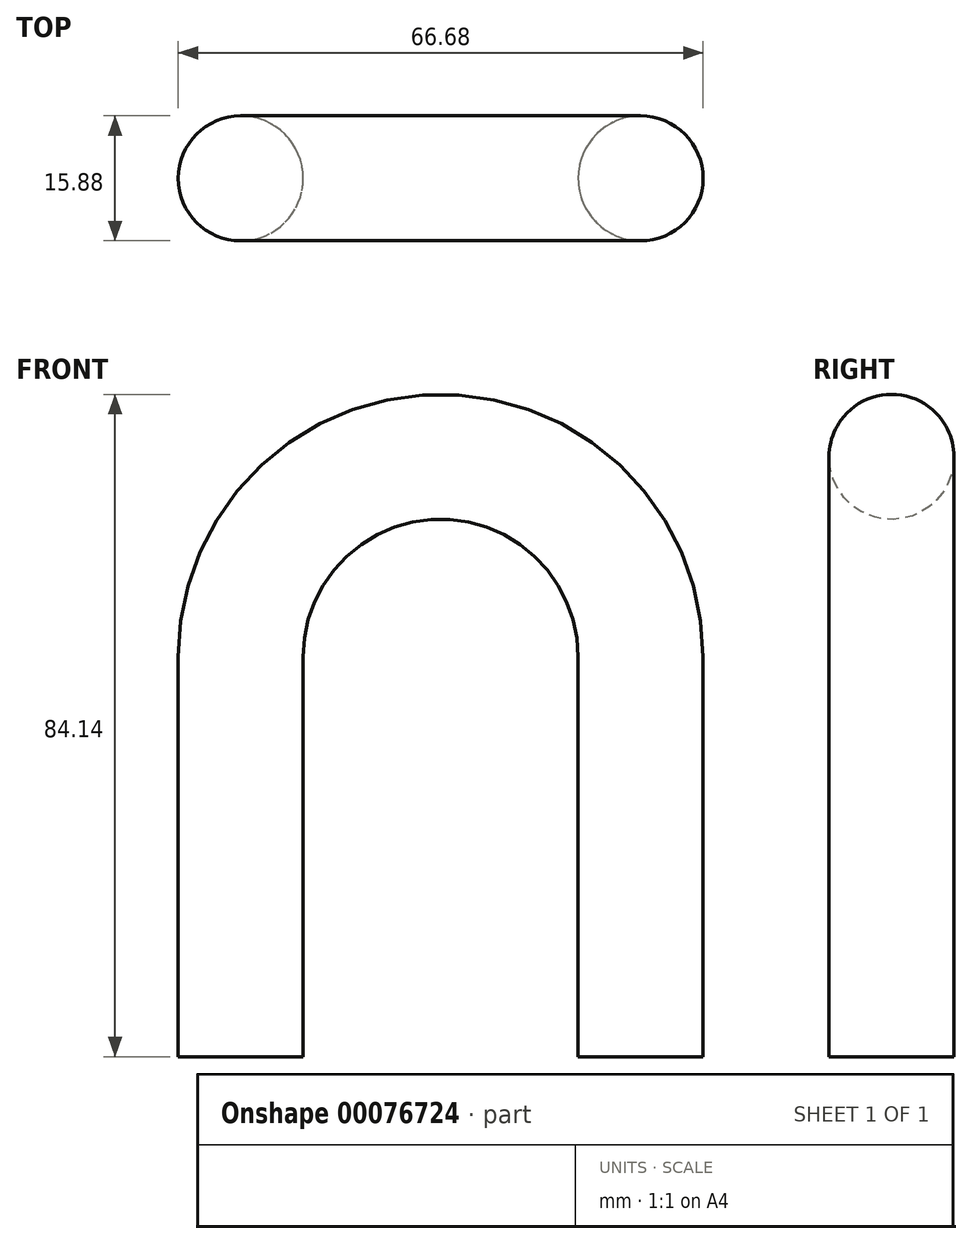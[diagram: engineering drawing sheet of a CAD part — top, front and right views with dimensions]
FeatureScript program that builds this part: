
annotation { "Feature Type Name" : "Feature", "Feature Type Description" : "" }
export const myFeature = defineFeature(function(context is Context, id is Id, definition is map)
    precondition{}
    {
        {
            var Q0;
            Q0=qCreatedBy(makeId("Top.planeOp"),FACE);
            var sketch = newSketch(context, id + "F0", { "sketchPlane" : qUnion([Q0])});
            skLineSegment(sketch, "E0", {"start": v(0, 0) * mm, "end": v(25.4, 0) * mm});
            skCircle(sketch, "E1", {"center": v(25.4, 0) * mm, "radius": 7.94 * mm});
            skSolve(sketch);
        }
        {
            var Q0;
            Q0=qCreatedBy(makeId("Front.planeOp"),FACE);
            var sketch = newSketch(context, id + "F1", { "sketchPlane" : qUnion([Q0])});
            skPoint(sketch, "E2.0", {"position": v(25.4, 0) * mm});
            skLineSegment(sketch, "E3", {"start": v(25.4, 0) * mm, "end": v(25.4, 50.8) * mm});
            skLineSegment(sketch, "E4", {"start": v(0, 0) * mm, "end": v(0, 76.2) * mm});
            skArc(sketch, "E5", {"start": v(25.4, 50.8) * mm, "mid": v(17.96, 68.76) * mm, "end": v(0, 76.2) * mm});
            skSolve(sketch);
        }
        {
            var Q0;
            Q0=makeQuery(id+"F0.imprint","IMPRINT",FACE,{"disambiguationData":[TD([[makeQuery(id+"F0.imprint","IMPRINT",EDGE,{"derivedFrom":sQuery(id+"F0.wireOp",EDGE,"E1")}),1.0]])]});
            var Q1;
            Q1=sQuery(id+"F1.wireOp",EDGE,"E3");
            var Q2;
            Q2=sQuery(id+"F1.wireOp",EDGE,"E5");
            sweep(context, id + "F2", {"profiles" : qUnion([Q0]), "path" : qUnion([Q1, Q2])});
        }
        {
            var Q0;
            Q0=makeQuery(id+"F2.opSweep","SWEPT_BODY",BODY,{"disambiguationData":[OSD([sQuery(id+"F0.wireOp",EDGE,"E1"),sQuery(id+"F1.wireOp",EDGE,"E5")])]});
            var Q1;
            Q1=makeQuery(id+"F2.opSweep","CAP_FACE",FACE,{"disambiguationData":[OSD([sQuery(id+"F0.wireOp",EDGE,"E1"),sQuery(id+"F1.wireOp",VERTEX,"E5.end")])],"isStart":false});
            mirror(context, id + "F3", {"operationType" : NewBodyOperationType.ADD, "entities" : qUnion([Q0]), "mirrorPlane" : qUnion([Q1])});
        }
    });
